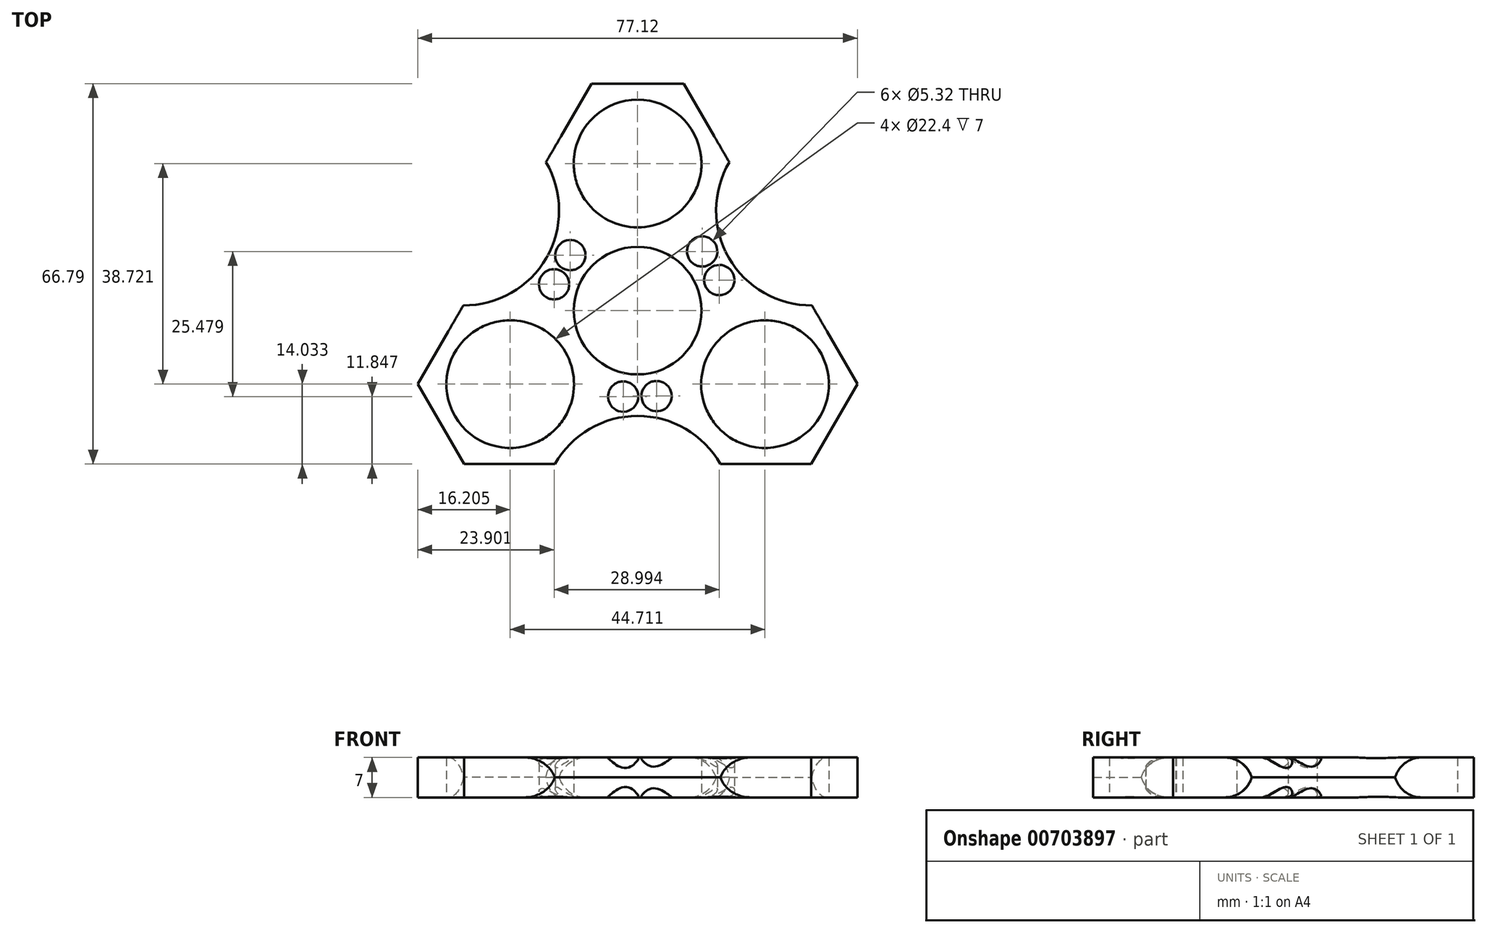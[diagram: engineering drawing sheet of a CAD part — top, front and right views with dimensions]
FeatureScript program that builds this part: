
annotation { "Feature Type Name" : "Feature", "Feature Type Description" : "" }
export const myFeature = defineFeature(function(context is Context, id is Id, definition is map)
    precondition{}
    {
        {
            var Q0;
            Q0=qCreatedBy(makeId("Top.planeOp"),FACE);
            var sketch = newSketch(context, id + "F0", { "sketchPlane" : qUnion([Q0])});
            skCircle(sketch, "E0", {"center": v(0, 0) * mm, "radius": 11.2 * mm});
            skCircle(sketch, "E1", {"center": v(0, 25.81) * mm, "radius": 11.2 * mm});
            skCircle(sketch, "E2.cCircle", {"center": v(0, 25.81) * mm, "radius": 14.04 * mm, "construction": true});
            skLineSegment(sketch, "E2.0", {"start": v(-8.1, 39.85) * mm, "end": v(8.1, 39.85) * mm});
            skLineSegment(sketch, "E2.1", {"start": v(8.1, 39.85) * mm, "end": v(16.2, 25.81) * mm});
            skLineSegment(sketch, "E2.2", {"start": v(16.2, 25.81) * mm, "end": v(8.1, 11.78) * mm});
            skLineSegment(sketch, "E2.3", {"start": v(8.1, 11.78) * mm, "end": v(-8.1, 11.78) * mm});
            skLineSegment(sketch, "E2.4", {"start": v(-8.1, 11.78) * mm, "end": v(-16.2, 25.81) * mm});
            skLineSegment(sketch, "E2.5", {"start": v(-16.2, 25.81) * mm, "end": v(-8.1, 39.85) * mm});
            skPoint(sketch, "E2.0.midPoint", {"position": v(0, 39.85) * mm});
            skCircle(sketch, "E3.1.0", {"center": v(-22.36, -12.9) * mm, "radius": 11.2 * mm});
            skCircle(sketch, "E3.2.0", {"center": v(22.36, -12.9) * mm, "radius": 11.2 * mm});
            skLineSegment(sketch, "E4.1.0", {"start": v(-38.56, -12.9) * mm, "end": v(-30.46, 1.13) * mm});
            skLineSegment(sketch, "E4.1.1", {"start": v(-30.46, -26.94) * mm, "end": v(-38.56, -12.9) * mm});
            skLineSegment(sketch, "E4.1.2", {"start": v(-14.25, -26.94) * mm, "end": v(-30.46, -26.94) * mm});
            skLineSegment(sketch, "E4.1.3", {"start": v(-6.15, -12.9) * mm, "end": v(-14.25, -26.94) * mm});
            skLineSegment(sketch, "E4.1.4", {"start": v(-14.25, 1.13) * mm, "end": v(-6.15, -12.9) * mm});
            skLineSegment(sketch, "E4.1.5", {"start": v(-30.46, 1.13) * mm, "end": v(-14.25, 1.13) * mm});
            skLineSegment(sketch, "E4.2.0", {"start": v(30.46, -26.94) * mm, "end": v(14.25, -26.94) * mm});
            skLineSegment(sketch, "E4.2.1", {"start": v(38.56, -12.9) * mm, "end": v(30.46, -26.94) * mm});
            skLineSegment(sketch, "E4.2.2", {"start": v(30.46, 1.13) * mm, "end": v(38.56, -12.9) * mm});
            skLineSegment(sketch, "E4.2.3", {"start": v(14.25, 1.13) * mm, "end": v(30.46, 1.13) * mm});
            skLineSegment(sketch, "E4.2.4", {"start": v(6.15, -12.9) * mm, "end": v(14.25, 1.13) * mm});
            skLineSegment(sketch, "E4.2.5", {"start": v(14.25, -26.94) * mm, "end": v(6.15, -12.9) * mm});
            skArc(sketch, "E5", {"start": v(-30.46, 1.13) * mm, "mid": v(-16.2, 9.36) * mm, "end": v(-16.2, 25.81) * mm});
            skArc(sketch, "E6.1.0", {"start": v(14.25, -26.94) * mm, "mid": v(0, -18.72) * mm, "end": v(-14.25, -26.94) * mm});
            skArc(sketch, "E6.2.0", {"start": v(16.2, 25.81) * mm, "mid": v(16.2, 9.36) * mm, "end": v(30.46, 1.13) * mm});
            skCircle(sketch, "E7", {"center": v(-14.66, 4.62) * mm, "radius": 2.66 * mm});
            skCircle(sketch, "E8", {"center": v(-11.8, 9.74) * mm, "radius": 2.66 * mm});
            skCircle(sketch, "E9.1.0", {"center": v(-2.53, -15.1) * mm, "radius": 2.66 * mm});
            skCircle(sketch, "E9.1.1", {"center": v(3.33, -15) * mm, "radius": 2.66 * mm});
            skCircle(sketch, "E9.2.0", {"center": v(14.34, 5.36) * mm, "radius": 2.66 * mm});
            skCircle(sketch, "E9.2.1", {"center": v(11.33, 10.39) * mm, "radius": 2.66 * mm});
            skSolve(sketch);
        }
        {
            var Q0;
            Q0=makeQuery(id+"F0.imprint","IMPRINT",FACE,{"disambiguationData":[TD([[makeQuery(id+"F0.imprint","IMPRINT",EDGE,{"derivedFrom":sQuery(id+"F0.wireOp",EDGE,"E0")}),-1.0]])]});
            var Q1;
            Q1=makeQuery(id+"F0.imprint","IMPRINT",FACE,{"disambiguationData":[TD([[makeQuery(id+"F0.imprint","IMPRINT",EDGE,{"derivedFrom":sQuery(id+"F0.wireOp",EDGE,"E3.1.0")}),-1.0]])]});
            var Q2;
            Q2=makeQuery(id+"F0.imprint","IMPRINT",FACE,{"disambiguationData":[TD([[makeQuery(id+"F0.imprint","IMPRINT",EDGE,{"derivedFrom":sQuery(id+"F0.wireOp",EDGE,"E1")}),-1.0]])]});
            var Q3;
            Q3=makeQuery(id+"F0.imprint","IMPRINT",FACE,{"disambiguationData":[TD([[makeQuery(id+"F0.imprint","IMPRINT",EDGE,{"derivedFrom":sQuery(id+"F0.wireOp",EDGE,"E3.2.0")}),-1.0]])]});
            extrude(context, id + "F1", {"entities" : qUnion([Q0, Q1, Q2, Q3]), "depth" : 7 * mm, "offsetDistance" : 25 * mm});
        }
        {
            var Q0;
            Q0=makeQuery(id+"F1.opExtrude","CAP_EDGE",EDGE,{"disambiguationData":[OSD([sQuery(id+"F0.wireOp",EDGE,"E6.1.0")])],"isStart":true});
            var Q1;
            Q1=makeQuery(id+"F1.opExtrude","CAP_EDGE",EDGE,{"disambiguationData":[OSD([sQuery(id+"F0.wireOp",EDGE,"E5")])],"isStart":true});
            var Q2;
            Q2=makeQuery(id+"F1.opExtrude","CAP_EDGE",EDGE,{"disambiguationData":[OSD([sQuery(id+"F0.wireOp",EDGE,"E5")])],"isStart":false});
            var Q3;
            Q3=makeQuery(id+"F1.opExtrude","CAP_EDGE",EDGE,{"disambiguationData":[OSD([sQuery(id+"F0.wireOp",EDGE,"E6.1.0")])],"isStart":false});
            fillet(context, id + "F2", {"entities" : qUnion([Q0, Q1, Q2, Q3]), "radius" : 5 * mm, "tangentPropagation" : true, "allowEdgeOverflow" : false});
        }
        {
            var Q0;
            Q0=makeQuery(id+"F1.opExtrude","CAP_EDGE",EDGE,{"disambiguationData":[OSD([sQuery(id+"F0.wireOp",EDGE,"E6.2.0")])],"isStart":false});
            var Q1;
            Q1=makeQuery(id+"F1.opExtrude","CAP_EDGE",EDGE,{"disambiguationData":[OSD([sQuery(id+"F0.wireOp",EDGE,"E6.2.0")])],"isStart":true});
            fillet(context, id + "F3", {"entities" : qUnion([Q0, Q1]), "radius" : 5 * mm, "tangentPropagation" : true, "allowEdgeOverflow" : false});
        }
    });
